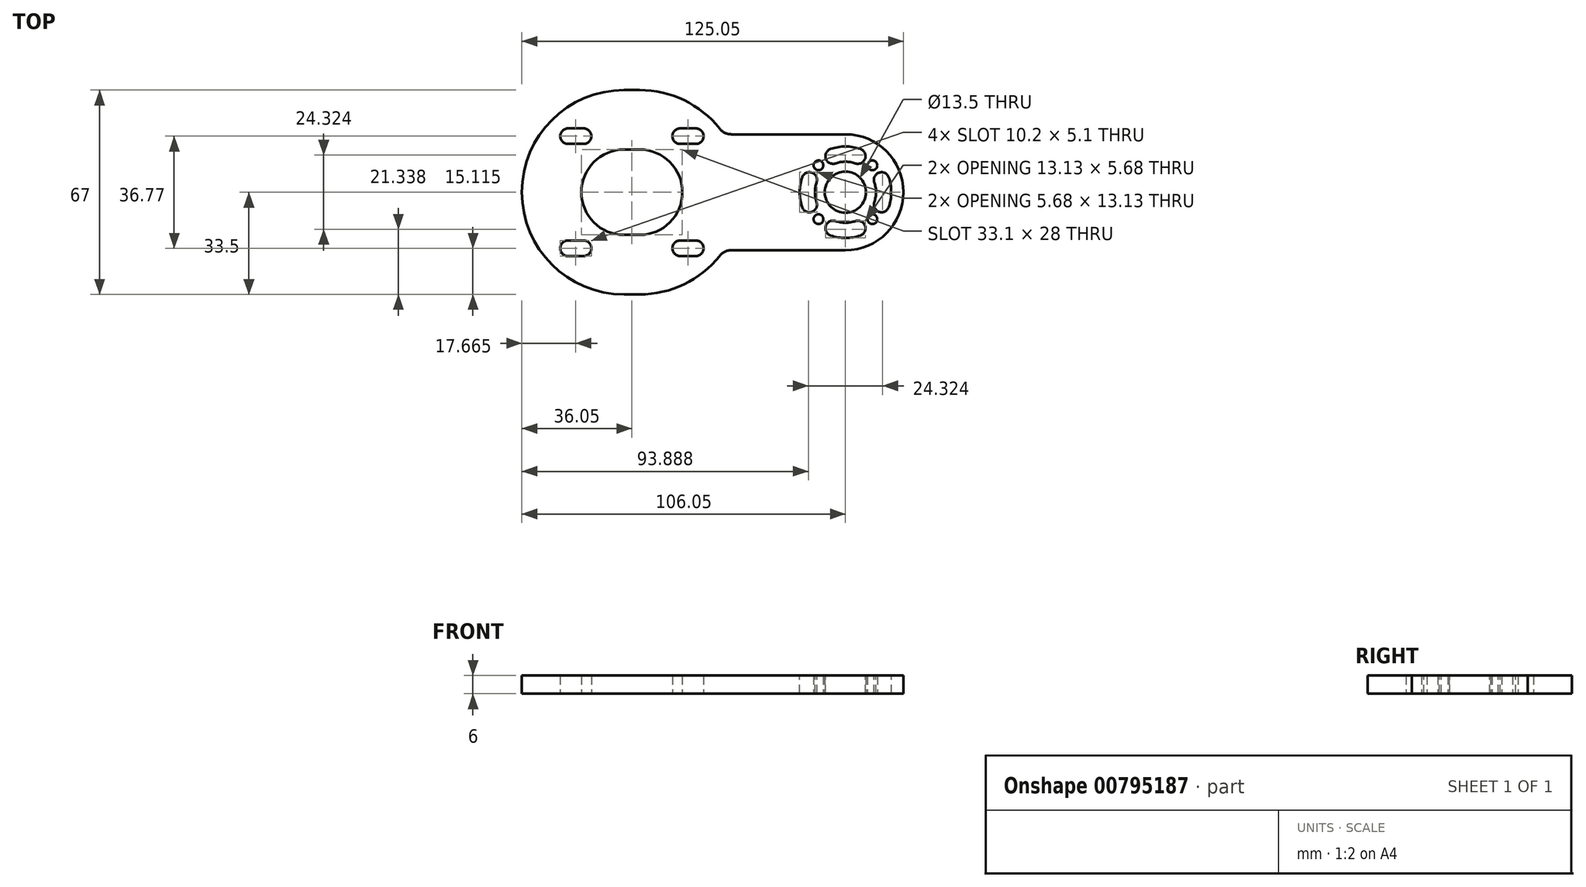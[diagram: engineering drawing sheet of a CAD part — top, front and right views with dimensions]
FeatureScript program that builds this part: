
annotation { "Feature Type Name" : "Feature", "Feature Type Description" : "" }
export const myFeature = defineFeature(function(context is Context, id is Id, definition is map)
    precondition{}
    {
        {
            var Q0;
            Q0=qCreatedBy(makeId("Top.planeOp"),FACE);
            var sketch = newSketch(context, id + "F0", { "sketchPlane" : qUnion([Q0])});
            skLineSegment(sketch, "E0.left", {"start": v(0, 33.5) * mm, "end": v(0, -16.5) * mm, "construction": true});
            skLineSegment(sketch, "E0.right", {"start": v(90, 33.5) * mm, "end": v(90, -16.5) * mm});
            skCircle(sketch, "E1", {"center": v(70, 0) * mm, "radius": 6.75 * mm, "construction": true});
            skArc(sketch, "E2", {"start": v(70, -19) * mm, "mid": v(89, 0) * mm, "end": v(70, 19) * mm});
            skLineSegment(sketch, "E3.bottom", {"start": v(45.4, -41.12) * mm, "end": v(-45.4, -41.12) * mm, "construction": true});
            skLineSegment(sketch, "E3.top", {"start": v(45.4, 41.12) * mm, "end": v(-45.4, 41.12) * mm, "construction": true});
            skLineSegment(sketch, "E3.right", {"start": v(-45.4, -41.12) * mm, "end": v(-45.4, 41.12) * mm, "construction": true});
            skPoint(sketch, "E3.middle", {"position": v(0, 0) * mm});
            skCircle(sketch, "E4", {"center": v(70, 0) * mm, "radius": 6.75 * mm});
            skLineSegment(sketch, "E5", {"start": v(70, 0) * mm, "end": v(61.16, 8.84) * mm, "construction": true});
            skCircle(sketch, "E6", {"center": v(61.16, 8.84) * mm, "radius": 1.6 * mm});
            skCircle(sketch, "E7.1.0", {"center": v(61.16, -8.84) * mm, "radius": 1.6 * mm});
            skCircle(sketch, "E7.2.0", {"center": v(78.84, -8.84) * mm, "radius": 1.6 * mm});
            skCircle(sketch, "E7.3.0", {"center": v(78.84, 8.84) * mm, "radius": 1.6 * mm});
            skLineSegment(sketch, "E8", {"start": v(61.16, 8.84) * mm, "end": v(66.16, 8.84) * mm});
            skLineSegment(sketch, "E9", {"start": v(61.16, -8.84) * mm, "end": v(66.16, -8.84) * mm});
            skLineSegment(sketch, "E10", {"start": v(78.84, -8.84) * mm, "end": v(83.84, -8.84) * mm});
            skLineSegment(sketch, "E11", {"start": v(78.84, 8.84) * mm, "end": v(83.84, 8.84) * mm});
            skLineSegment(sketch, "E12", {"start": v(70, 0) * mm, "end": v(75, 0) * mm});
            skArc(sketch, "E13.0.startCap", {"start": v(78.84, 7.24) * mm, "mid": v(77.24, 8.84) * mm, "end": v(78.84, 10.44) * mm});
            skArc(sketch, "E13.0.endCap", {"start": v(83.84, 10.44) * mm, "mid": v(85.44, 8.84) * mm, "end": v(83.84, 7.24) * mm});
            skArc(sketch, "E14.0.startCap", {"start": v(61.16, 7.24) * mm, "mid": v(59.56, 8.84) * mm, "end": v(61.16, 10.44) * mm});
            skArc(sketch, "E14.1.startCap", {"start": v(61.16, -10.44) * mm, "mid": v(59.56, -8.84) * mm, "end": v(61.16, -7.24) * mm});
            skArc(sketch, "E14.2.startCap", {"start": v(78.84, -10.44) * mm, "mid": v(77.24, -8.84) * mm, "end": v(78.84, -7.24) * mm});
            skArc(sketch, "E14.2.endCap", {"start": v(83.84, -7.24) * mm, "mid": v(85.44, -8.84) * mm, "end": v(83.84, -10.44) * mm});
            skArc(sketch, "E15.0.startCap", {"start": v(70, -6.75) * mm, "mid": v(63.25, 0) * mm, "end": v(70, 6.75) * mm});
            skArc(sketch, "E15.0.endCap", {"start": v(75, 6.75) * mm, "mid": v(81.75, 0) * mm, "end": v(75, -6.75) * mm});
            skArc(sketch, "E16", {"start": v(75, -19) * mm, "mid": v(94, 0) * mm, "end": v(75, 19) * mm, "construction": true});
            skLineSegment(sketch, "E17", {"start": v(75, 19) * mm, "end": v(32.65, 19) * mm});
            skLineSegment(sketch, "E18", {"start": v(75, -19) * mm, "end": v(32.65, -19) * mm});
            skPoint(sketch, "E19.visualSharp", {"position": v(27.6, 19) * mm});
            skCircle(sketch, "E20", {"center": v(0, 0) * mm, "radius": 26 * mm, "construction": true});
            skCircle(sketch, "E21", {"center": v(0, 0) * mm, "radius": 16 * mm, "construction": true});
            skLineSegment(sketch, "E22", {"start": v(0, 0) * mm, "end": v(-28.53, 28.53) * mm, "construction": true});
            skCircle(sketch, "E23", {"center": v(-18.38, 18.38) * mm, "radius": 2.55 * mm, "construction": true});
            skCircle(sketch, "E24.1.0", {"center": v(-18.38, -18.38) * mm, "radius": 2.55 * mm, "construction": true});
            skCircle(sketch, "E24.2.0", {"center": v(18.38, -18.38) * mm, "radius": 2.55 * mm, "construction": true});
            skCircle(sketch, "E24.3.0", {"center": v(18.38, 18.38) * mm, "radius": 2.55 * mm, "construction": true});
            skLineSegment(sketch, "E25", {"start": v(15.83, 18.38) * mm, "end": v(20.93, 18.38) * mm});
            skLineSegment(sketch, "E26", {"start": v(15.83, -18.38) * mm, "end": v(20.93, -18.38) * mm});
            skLineSegment(sketch, "E27", {"start": v(-20.93, -18.38) * mm, "end": v(-15.83, -18.38) * mm});
            skLineSegment(sketch, "E28", {"start": v(-20.93, 18.38) * mm, "end": v(-15.83, 18.38) * mm});
            skArc(sketch, "E29.0.startCap", {"start": v(-20.93, 15.83) * mm, "mid": v(-23.48, 18.38) * mm, "end": v(-20.93, 20.93) * mm});
            skArc(sketch, "E29.0.endCap", {"start": v(-15.83, 20.93) * mm, "mid": v(-13.28, 18.38) * mm, "end": v(-15.83, 15.83) * mm});
            skLineSegment(sketch, "E29.0.left", {"start": v(-20.93, 20.93) * mm, "end": v(-15.83, 20.93) * mm});
            skLineSegment(sketch, "E29.0.right", {"start": v(-20.93, 15.83) * mm, "end": v(-15.83, 15.83) * mm});
            skArc(sketch, "E30.0.startCap", {"start": v(15.83, 15.83) * mm, "mid": v(13.28, 18.38) * mm, "end": v(15.83, 20.93) * mm});
            skArc(sketch, "E30.0.endCap", {"start": v(20.93, 20.93) * mm, "mid": v(23.48, 18.38) * mm, "end": v(20.93, 15.83) * mm});
            skLineSegment(sketch, "E30.0.left", {"start": v(15.83, 20.93) * mm, "end": v(20.93, 20.93) * mm});
            skLineSegment(sketch, "E30.0.right", {"start": v(15.83, 15.83) * mm, "end": v(20.93, 15.83) * mm});
            skArc(sketch, "E31.0.startCap", {"start": v(15.83, -20.93) * mm, "mid": v(13.28, -18.38) * mm, "end": v(15.83, -15.83) * mm});
            skArc(sketch, "E31.0.endCap", {"start": v(20.93, -15.83) * mm, "mid": v(23.48, -18.38) * mm, "end": v(20.93, -20.93) * mm});
            skLineSegment(sketch, "E31.0.left", {"start": v(15.83, -15.83) * mm, "end": v(20.93, -15.83) * mm});
            skLineSegment(sketch, "E31.0.right", {"start": v(15.83, -20.93) * mm, "end": v(20.93, -20.93) * mm});
            skArc(sketch, "E32.0.startCap", {"start": v(-20.93, -20.93) * mm, "mid": v(-23.48, -18.38) * mm, "end": v(-20.93, -15.83) * mm});
            skArc(sketch, "E32.0.endCap", {"start": v(-15.83, -15.83) * mm, "mid": v(-13.28, -18.38) * mm, "end": v(-15.83, -20.93) * mm});
            skLineSegment(sketch, "E32.0.left", {"start": v(-20.93, -15.83) * mm, "end": v(-15.83, -15.83) * mm});
            skLineSegment(sketch, "E32.0.right", {"start": v(-20.93, -20.93) * mm, "end": v(-15.83, -20.93) * mm});
            skLineSegment(sketch, "E33", {"start": v(2.55, 0) * mm, "end": v(-2.55, 0) * mm});
            skArc(sketch, "E34.0.startCap", {"start": v(2.55, 14) * mm, "mid": v(16.55, 0) * mm, "end": v(2.55, -14) * mm});
            skArc(sketch, "E34.0.endCap", {"start": v(-2.55, -14) * mm, "mid": v(-16.55, 0) * mm, "end": v(-2.55, 14) * mm});
            skLineSegment(sketch, "E34.0.left", {"start": v(2.55, -14) * mm, "end": v(-2.55, -14) * mm});
            skLineSegment(sketch, "E34.0.right", {"start": v(2.55, 14) * mm, "end": v(-2.55, 14) * mm});
            skArc(sketch, "E35.0.startCap", {"start": v(2.55, 33.5) * mm, "mid": v(17.09, 30.18) * mm, "end": v(28.74, 20.88) * mm});
            skArc(sketch, "E35.0.endCap", {"start": v(-2.55, -33.5) * mm, "mid": v(-36.05, 0) * mm, "end": v(-2.55, 33.5) * mm});
            skLineSegment(sketch, "E35.0.left", {"start": v(2.55, -33.5) * mm, "end": v(-2.55, -33.5) * mm});
            skLineSegment(sketch, "E35.0.right", {"start": v(2.55, 33.5) * mm, "end": v(-2.55, 33.5) * mm});
            skArc(sketch, "E36.trimOffspring", {"start": v(28.74, -20.88) * mm, "mid": v(17.09, -30.18) * mm, "end": v(2.55, -33.5) * mm});
            skPoint(sketch, "E37.visualSharp", {"position": v(30.14, 19) * mm});
            skArc(sketch, "E37.filletArc", {"start": v(28.74, 20.88) * mm, "mid": v(30.48, 19.5) * mm, "end": v(32.65, 19) * mm});
            skPoint(sketch, "E38.visualSharp", {"position": v(30.14, -19) * mm});
            skArc(sketch, "E38.filletArc", {"start": v(32.65, -19) * mm, "mid": v(30.48, -19.5) * mm, "end": v(28.74, -20.88) * mm});
            skSolve(sketch);
        }
        {
            var Q0;
            Q0=qSketchRegion(id+"F0",true);
            extrude(context, id + "F1", {"entities" : qUnion([Q0]), "depth" : 6 * mm, "offsetDistance" : 25 * mm});
        }
        {
            var Q0;
            Q0=makeQuery(id+"F1.opExtrude","CAP_FACE",FACE,{"disambiguationData":[OSD([sQuery(id+"F0.wireOp",EDGE,"H2Rf1mUt-0jlt-27wB-YffO-BGlGPGkjmCcf"),sQuery(id+"F0.wireOp",EDGE,"pAdha1hi-vLvk-yrs3-a5r3-yK9QRZCf7Ppp"),sQuery(id+"F0.wireOp",EDGE,"E2"),sQuery(id+"F0.wireOp",EDGE,"E4"),sQuery(id+"F0.wireOp",EDGE,"E6"),sQuery(id+"F0.wireOp",EDGE,"E7.1.0"),sQuery(id+"F0.wireOp",EDGE,"E7.2.0"),sQuery(id+"F0.wireOp",EDGE,"E7.3.0"),sQuery(id+"F0.wireOp",EDGE,"E17"),sQuery(id+"F0.wireOp",EDGE,"E18"),sQuery(id+"F0.wireOp",EDGE,"E19.filletArc"),sQuery(id+"F0.wireOp",EDGE,"bb5d5ffc-c1ad-4c8e-af76-ad25ce88a9b4.filletArc"),sQuery(id+"F0.wireOp",EDGE,"E23"),sQuery(id+"F0.wireOp",EDGE,"E24.1.0"),sQuery(id+"F0.wireOp",EDGE,"E24.2.0"),sQuery(id+"F0.wireOp",EDGE,"E24.3.0")])],"isStart":false});
            var sketch = newSketch(context, id + "F2", { "sketchPlane" : qUnion([Q0])});
            skArc(sketch, "E39", {"start": v(58.18, 4.07) * mm, "mid": v(57.5, 0) * mm, "end": v(58.18, -4.07) * mm});
            skLineSegment(sketch, "E40", {"start": v(70, 0) * mm, "end": v(55.67, 4.93) * mm, "construction": true});
            skLineSegment(sketch, "E41", {"start": v(70, 0) * mm, "end": v(55.3, -5.06) * mm, "construction": true});
            skArc(sketch, "E42.0.startCap", {"start": v(55.82, 4.88) * mm, "mid": v(59, 6.43) * mm, "end": v(60.54, 3.26) * mm});
            skArc(sketch, "E42.0.endCap", {"start": v(60.54, -3.26) * mm, "mid": v(59, -6.43) * mm, "end": v(55.82, -4.88) * mm});
            skArc(sketch, "E42.0.left", {"start": v(60.54, 3.26) * mm, "mid": v(60, 0) * mm, "end": v(60.54, -3.26) * mm});
            skArc(sketch, "E42.0.right", {"start": v(55.82, 4.88) * mm, "mid": v(55, 0) * mm, "end": v(55.82, -4.88) * mm});
            skArc(sketch, "E43.1.0", {"start": v(65.12, -14.18) * mm, "mid": v(63.57, -11) * mm, "end": v(66.74, -9.46) * mm});
            skArc(sketch, "E43.1.1", {"start": v(66.74, -9.46) * mm, "mid": v(70, -10) * mm, "end": v(73.26, -9.46) * mm});
            skArc(sketch, "E43.1.2", {"start": v(73.26, -9.46) * mm, "mid": v(76.43, -11) * mm, "end": v(74.88, -14.18) * mm});
            skArc(sketch, "E43.1.3", {"start": v(65.12, -14.18) * mm, "mid": v(70, -15) * mm, "end": v(74.88, -14.18) * mm});
            skArc(sketch, "E43.2.0", {"start": v(84.18, -4.88) * mm, "mid": v(81, -6.43) * mm, "end": v(79.46, -3.26) * mm});
            skArc(sketch, "E43.2.1", {"start": v(79.46, -3.26) * mm, "mid": v(80, 0) * mm, "end": v(79.46, 3.26) * mm});
            skArc(sketch, "E43.2.2", {"start": v(79.46, 3.26) * mm, "mid": v(81, 6.43) * mm, "end": v(84.18, 4.88) * mm});
            skArc(sketch, "E43.2.3", {"start": v(84.18, -4.88) * mm, "mid": v(85, 0) * mm, "end": v(84.18, 4.88) * mm});
            skArc(sketch, "E43.3.0", {"start": v(74.88, 14.18) * mm, "mid": v(76.43, 11) * mm, "end": v(73.26, 9.46) * mm});
            skArc(sketch, "E43.3.1", {"start": v(73.26, 9.46) * mm, "mid": v(70, 10) * mm, "end": v(66.74, 9.46) * mm});
            skArc(sketch, "E43.3.2", {"start": v(66.74, 9.46) * mm, "mid": v(63.57, 11) * mm, "end": v(65.12, 14.18) * mm});
            skArc(sketch, "E43.3.3", {"start": v(74.88, 14.18) * mm, "mid": v(70, 15) * mm, "end": v(65.12, 14.18) * mm});
            skSolve(sketch);
        }
        {
            var Q0;
            Q0 = qSketchRegion(id + "F2", true);
            extrude(context, id + "F3", {"entities" : qUnion([Q0]), "operationType" : NewBodyOperationType.REMOVE, "oppositeDirection" : true, "depth" : 25 * mm, "offsetDistance" : 25 * mm});
        }
    });
